# Revit family: ROSENBERG_KBA
name_source: partatom
category: Wyposażenie mechaniczne
revit_build: Autodesk Revit 2017 (Build: 20160225_1515(x64)
units: mm (PartAtom-declared; Revit-internal decimal feet)

## family parameters
Numer OmniClass = 23.75.00.00
Oparty na płaszczyźnie roboczej = Tak
Punkt obliczania pomieszczeń = Nie
Tnij formami wycięć po wczytaniu = Nie
Typ części = Normalny
Tytuł OmniClass = Climate Control (HVAC)
Współdzielony = Nie
Wymiar okrągłego złącza = Użyj średnicy
Zawsze pionowo = Tak

## types (20) — shared parameters
Base_height = 29 mm  [stored 0.0951444 ft]
Base_width = 38 mm  [stored 0.124672 ft]
Box = 140 mm  [stored 0.459318 ft]
Date = 10.2018
Domyślna rzędna = 1219 mm
Frequency = 50 Hz
Holder = 55 mm  [stored 0.180446 ft]
Hole_3 = 5 mm  [stored 0.0164042 ft]
Hole_lb = 10
Material = <Wg kategorii>
Opis = Kitchen exhaust fan
Producent = Rosenberg
Protection class = IP54
URL = https://www.rosenberg.pl
Version = 1
Width_hatch = 60 mm  [stored 0.19685 ft]

## per-type parameters (varying)
| type | Connector_height | Current | Depth | Depth_box | Diameter_connector | Diameter_hole | Height | Hole | Inlet_X | Inlet_Y | Length_base | Length_hole | Model | Offset | Outlet_X | Outlet_Y | Outlet_height | Power | Visibility_1 | Visibility_2 | Voltage | Weight | Width |
| 315-4SW.098_400V | 45 mm  [stored 0.147638 ft] | 0 A | 307 mm | 496 mm | 315 mm | 305 mm | 600 mm | 280 mm | 398 mm | 339 mm | 800 mm | 51 mm | 315-4SW.098 | 35 mm  [stored 0.114829 ft] | 154 mm | 188 mm | 45 mm  [stored 0.147638 ft] | 160 W | Tak | Nie | 400 V | 77.00 kg | 690 mm |
| 400-4SW.120_400V | 45 mm  [stored 0.147638 ft] | 1 A | 331 mm | 492 mm | 355 mm | 345 mm | 665 mm | 310 mm | 451 mm | 372 mm | 800 mm | 51 mm | 400-4SW.120 | 35 mm  [stored 0.114829 ft] | 163 mm | 207 mm | 45 mm  [stored 0.147638 ft] | 400 W | Tak | Nie | 400 V | 71.00 kg | 770 mm |
| 355-4SW.110_400V | 45 mm  [stored 0.147638 ft] | 1 A | 331 mm | 472 mm | 355 mm | 345 mm | 665 mm | 290 mm | 451 mm | 372 mm | 800 mm | 51 mm | 355-4SW.110 | 35 mm  [stored 0.114829 ft] | 163 mm | 207 mm | 45 mm  [stored 0.147638 ft] | 285 W | Tak | Nie | 400 V | 70.00 kg | 770 mm |
| 355-2SW.110_400V | 45 mm  [stored 0.147638 ft] | 4 A | 331 mm | 520 mm | 355 mm | 345 mm | 665 mm | 290 mm | 451 mm | 372 mm | 800 mm | 51 mm | 355-2SW.110 | 35 mm  [stored 0.114829 ft] | 163 mm | 207 mm | 45 mm  [stored 0.147638 ft] | 2060 W | Tak | Nie | 400 V | 77.00 kg | 770 mm |
| 315-2SW.098_400V | 45 mm  [stored 0.147638 ft] | 2 A | 307 mm | 496 mm | 315 mm | 305 mm | 600 mm | 280 mm | 398 mm | 339 mm | 800 mm | 51 mm | 315-2SW.098 | 35 mm  [stored 0.114829 ft] | 154 mm | 188 mm | 45 mm  [stored 0.147638 ft] | 1300 W | Tak | Nie | 400 V | 77.00 kg | 690 mm |
| 280-4ST.114_400V | 45 mm  [stored 0.147638 ft] | 3 A | 291 mm | 480 mm | 280 mm | 270 mm  [stored 0.885827 ft] | 537 mm | 270 mm  [stored 0.885827 ft] | 360 mm | 295 mm | 600 mm | 51 mm | 280-4ST.114 | 35 mm  [stored 0.114829 ft] | 143 mm | 172 mm | 45 mm  [stored 0.147638 ft] | 1750 W | Tak | Nie | 400 V | 64.00 kg | 625 mm |
| 250-4ST.102_400V | 45 mm  [stored 0.147638 ft] | 3 A | 272 mm | 461 mm | 250 mm  [stored 0.82021 ft] | 240 mm  [stored 0.787402 ft] | 500 mm | 240 mm  [stored 0.787402 ft] | 333 mm | 282 mm | 600 mm | 51 mm | 250-4ST.102 | 35 mm  [stored 0.114829 ft] | 133 mm | 162 mm | 45 mm  [stored 0.147638 ft] | 1180 W | Tak | Nie | 400 V | 56.00 kg | 576 mm |
| 225-4ST.092_400V | 45 mm  [stored 0.147638 ft] | 1 A | 251 mm  [stored 0.823491 ft] | 413 mm | 225 mm  [stored 0.738189 ft] | 215 mm | 445 mm | 215 mm | 301 mm | 256 mm  [stored 0.839895 ft] | 600 mm | 51 mm | 225-4ST.092 | 35 mm  [stored 0.114829 ft] | 123 mm | 147 mm | 45 mm  [stored 0.147638 ft] | 420 W | Tak | Nie | 400 V | 37.00 kg | 522 mm |
| 200-4ST.082_400V | 45 mm  [stored 0.147638 ft] | 1 A | 232 mm  [stored 0.761155 ft] | 373 mm | 200 mm  [stored 0.656168 ft] | 190 mm | 445 mm | 190 mm | 292 mm | 249 mm  [stored 0.816929 ft] | 450 mm | 51 mm | 200-4ST.082 | 35 mm  [stored 0.114829 ft] | 113 mm  [stored 0.370735 ft] | 143 mm | 45 mm  [stored 0.147638 ft] | 375 W | Tak | Nie | 400 V | 31.50 kg | 510 mm |
| 180-4ST.082_400V | 45 mm  [stored 0.147638 ft] | 1 A | 221 mm  [stored 0.725066 ft] | 362 mm | 200 mm  [stored 0.656168 ft] | 190 mm | 412 mm | 170 mm  [stored 0.557743 ft] | 269 mm  [stored 0.882546 ft] | 230 mm  [stored 0.754593 ft] | 450 mm | 60 mm  [stored 0.19685 ft] | 180-4ST.082 | 35 mm  [stored 0.114829 ft] | 107 mm  [stored 0.35105 ft] | 135 mm | 45 mm  [stored 0.147638 ft] | 220 W | Tak | Nie | 400 V | 31.50 kg | 470 mm |
| 450-4SW.138_400V | 80 mm  [stored 0.262467 ft] | 2 A | 415 mm | 603 mm | 450 mm | 440 mm | 800 mm | 310 mm | 511 mm | 450 mm | 800 mm | 51 mm | 450-4SW.138 | 80 mm  [stored 0.262467 ft] | 163 mm | 207 mm | 80 mm  [stored 0.262467 ft] | 910 W | Nie | Tak | 400 V | 92.00 kg | 900 mm |
| 180-4ST.082 | 45 mm  [stored 0.147638 ft] | 1 A | 221 mm  [stored 0.725066 ft] | 362 mm | 200 mm  [stored 0.656168 ft] | 190 mm | 412 mm | 170 mm  [stored 0.557743 ft] | 269 mm  [stored 0.882546 ft] | 230 mm  [stored 0.754593 ft] | 450 mm | 60 mm  [stored 0.19685 ft] | 180-4ST.082 | 35 mm  [stored 0.114829 ft] | 107 mm  [stored 0.35105 ft] | 134 mm | 45 mm  [stored 0.147638 ft] | 240 W | Tak | Nie | 230 V | 31.50 kg | 470 mm |
| 200-4ST.082 | 45 mm  [stored 0.147638 ft] | 1 A | 232 mm  [stored 0.761155 ft] | 373 mm | 200 mm  [stored 0.656168 ft] | 190 mm | 445 mm | 190 mm | 292 mm | 249 mm  [stored 0.816929 ft] | 450 mm | 51 mm | 200-4ST.082 | 35 mm  [stored 0.114829 ft] | 113 mm  [stored 0.370735 ft] | 143 mm | 45 mm  [stored 0.147638 ft] | 310 W | Tak | Nie | 230 V | 31.50 kg | 510 mm |
| 225-4ST.092 | 45 mm  [stored 0.147638 ft] | 1 A | 251 mm  [stored 0.823491 ft] | 413 mm | 225 mm  [stored 0.738189 ft] | 215 mm | 445 mm | 215 mm | 301 mm | 256 mm  [stored 0.839895 ft] | 600 mm | 51 mm | 225-4ST.092 | 35 mm  [stored 0.114829 ft] | 123 mm | 147 mm | 45 mm  [stored 0.147638 ft] | 420 W | Tak | Nie | 400 V | 37.00 kg | 522 mm |
| 250-4ST.102 | 45 mm  [stored 0.147638 ft] | 3 A | 272 mm | 461 mm | 250 mm  [stored 0.82021 ft] | 240 mm  [stored 0.787402 ft] | 500 mm | 240 mm  [stored 0.787402 ft] | 333 mm | 282 mm | 600 mm | 51 mm | 250-4ST.102 | 35 mm  [stored 0.114829 ft] | 133 mm | 162 mm | 45 mm  [stored 0.147638 ft] | 1180 W | Tak | Nie | 400 V | 56.00 kg | 576 mm |
| 280-4ST.114 | 60 mm  [stored 0.19685 ft] | 6 A | 291 mm | 480 mm | 280 mm | 270 mm  [stored 0.885827 ft] | 537 mm | 270 mm  [stored 0.885827 ft] | 360 mm | 295 mm | 600 mm | 51 mm | 280-4ST.114 | 35 mm  [stored 0.114829 ft] | 143 mm | 172 mm | 60 mm  [stored 0.19685 ft] | 1400 W | Tak | Nie | 230 V | 64.00 kg | 625 mm |
| 315-4SW.098 | 60 mm  [stored 0.19685 ft] | 1 A | 307 mm | 496 mm | 315 mm | 305 mm | 600 mm | 280 mm | 398 mm | 339 mm | 800 mm | 51 mm | 315-4SW.098 | 35 mm  [stored 0.114829 ft] | 154 mm | 188 mm | 60 mm  [stored 0.19685 ft] | 200 W | Tak | Nie | 230 V | 67.00 kg | 690 mm |
| 355-4SW.110 | 60 mm  [stored 0.19685 ft] | 1 A | 331 mm | 472 mm | 355 mm | 345 mm | 665 mm | 290 mm | 451 mm | 372 mm | 800 mm | 51 mm | 355-4SW.110 | 35 mm  [stored 0.114829 ft] | 163 mm | 207 mm | 60 mm  [stored 0.19685 ft] | 290 W | Tak | Nie | 230 V | 70.00 kg | 770 mm |
| 400-4SW.120 | 60 mm  [stored 0.19685 ft] | 2 A | 331 mm | 492 mm | 355 mm | 345 mm | 665 mm | 310 mm | 451 mm | 372 mm | 800 mm | 51 mm | 400-4SW.120 | 35 mm  [stored 0.114829 ft] | 163 mm | 207 mm | 60 mm  [stored 0.19685 ft] | 450 W | Tak | Nie | 230 V | 71.00 kg | 770 mm |
| 500-4SW.138_400V | 80 mm  [stored 0.262467 ft] | 3 A | 415 mm | 603 mm | 450 mm | 440 mm | 800 mm | 310 mm | 511 mm | 450 mm | 800 mm | 51 mm | 500-4SW.138 | 80 mm  [stored 0.262467 ft] | 163 mm | 207 mm | 80 mm  [stored 0.262467 ft] | 1550 W | Nie | Tak | 400 V | 92.00 kg | 900 mm |

note: [stored X ft] marks values corroborated as IEEE doubles in the binary element streams (Revit-internal decimal feet)

## geometry (parser evidence)
native form markers: Blend x6, Sweep x7
no freeform markers — native parametric forms only
